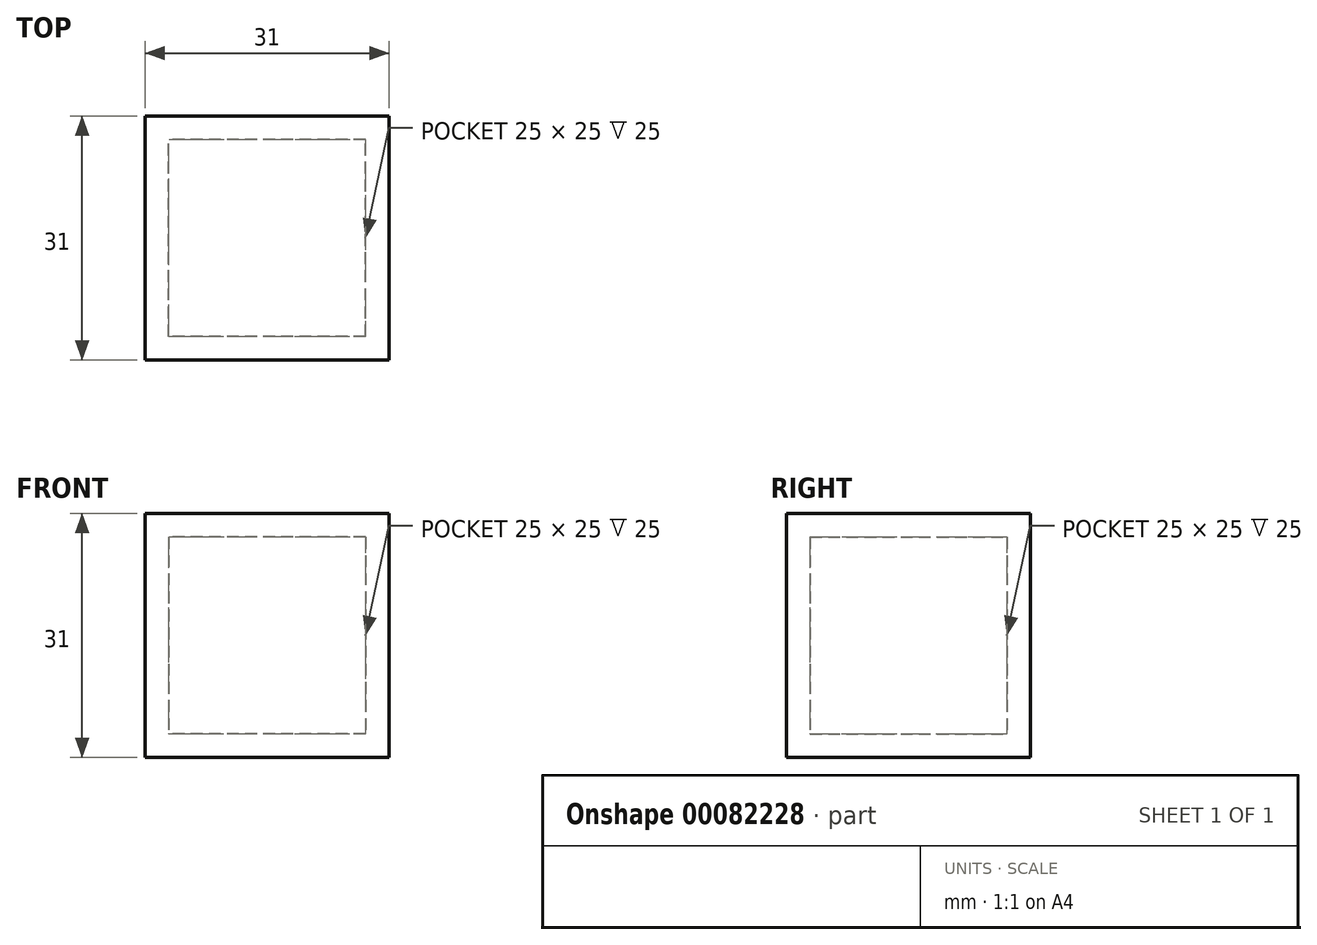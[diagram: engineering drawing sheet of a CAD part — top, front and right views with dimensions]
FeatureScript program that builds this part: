
annotation { "Feature Type Name" : "Feature", "Feature Type Description" : "" }
export const myFeature = defineFeature(function(context is Context, id is Id, definition is map)
    precondition{}
    {
        {
            var Q0;
            Q0=qCreatedBy(makeId("Front.planeOp"),FACE);
            var sketch = newSketch(context, id + "F0", { "sketchPlane" : qUnion([Q0])});
            skLineSegment(sketch, "E0.bottom", {"start": v(12.5, 12.5) * mm, "end": v(-12.5, 12.5) * mm});
            skLineSegment(sketch, "E0.top", {"start": v(12.5, -12.5) * mm, "end": v(-12.5, -12.5) * mm});
            skLineSegment(sketch, "E0.left", {"start": v(12.5, 12.5) * mm, "end": v(12.5, -12.5) * mm});
            skLineSegment(sketch, "E0.right", {"start": v(-12.5, 12.5) * mm, "end": v(-12.5, -12.5) * mm});
            skPoint(sketch, "E0.middle", {"position": v(0, 0) * mm});
            skLineSegment(sketch, "E1.bottom", {"start": v(15.5, 15.5) * mm, "end": v(-15.5, 15.5) * mm});
            skLineSegment(sketch, "E1.top", {"start": v(15.5, -15.5) * mm, "end": v(-15.5, -15.5) * mm});
            skLineSegment(sketch, "E1.left", {"start": v(15.5, 15.5) * mm, "end": v(15.5, -15.5) * mm});
            skLineSegment(sketch, "E1.right", {"start": v(-15.5, 15.5) * mm, "end": v(-15.5, -15.5) * mm});
            skSolve(sketch);
        }
        {
            var Q0;
            Q0 = qSketchRegion(id + "F0", true);
            extrude(context, id + "F1", {"entities" : qUnion([Q0]), "endBound" : BoundingType.SYMMETRIC, "depth" : 31 * mm});
        }
        {
            var Q0;
            Q0=makeQuery(id+"F1.opExtrude","CAP_FACE",FACE,{"disambiguationData":[OSD([sQuery(id+"F0.wireOp",EDGE,"E0.bottom"),sQuery(id+"F0.wireOp",EDGE,"E0.top"),sQuery(id+"F0.wireOp",EDGE,"E0.left"),sQuery(id+"F0.wireOp",EDGE,"E0.right"),sQuery(id+"F0.wireOp",EDGE,"E1.bottom"),sQuery(id+"F0.wireOp",EDGE,"E1.top"),sQuery(id+"F0.wireOp",EDGE,"E1.left"),sQuery(id+"F0.wireOp",EDGE,"E1.right")])],"isStart":false});
            var sketch = newSketch(context, id + "F2", { "sketchPlane" : qUnion([Q0])});
            skLineSegment(sketch, "E2.bottom", {"start": v(12.5, 12.5) * mm, "end": v(-12.5, 12.5) * mm});
            skLineSegment(sketch, "E2.top", {"start": v(12.5, -12.5) * mm, "end": v(-12.5, -12.5) * mm});
            skLineSegment(sketch, "E2.left", {"start": v(12.5, 12.5) * mm, "end": v(12.5, -12.5) * mm});
            skLineSegment(sketch, "E2.right", {"start": v(-12.5, 12.5) * mm, "end": v(-12.5, -12.5) * mm});
            skPoint(sketch, "E2.middle", {"position": v(0, 0) * mm});
            skSolve(sketch);
        }
        {
            var Q0;
            Q0 = qSketchRegion(id + "F2", true);
            extrude(context, id + "F3", {"entities" : qUnion([Q0]), "operationType" : NewBodyOperationType.ADD, "oppositeDirection" : true, "depth" : 3 * mm});
        }
        {
            var Q0;
            Q0=makeQuery(id+"F1.opExtrude","CAP_FACE",FACE,{"disambiguationData":[OSD([sQuery(id+"F0.wireOp",EDGE,"E0.bottom"),sQuery(id+"F0.wireOp",EDGE,"E0.top"),sQuery(id+"F0.wireOp",EDGE,"E0.left"),sQuery(id+"F0.wireOp",EDGE,"E0.right"),sQuery(id+"F0.wireOp",EDGE,"E1.bottom"),sQuery(id+"F0.wireOp",EDGE,"E1.top"),sQuery(id+"F0.wireOp",EDGE,"E1.left"),sQuery(id+"F0.wireOp",EDGE,"E1.right")])],"isStart":true});
            var sketch = newSketch(context, id + "F4", { "sketchPlane" : qUnion([Q0])});
            skLineSegment(sketch, "E3.bottom", {"start": v(12.5, 12.5) * mm, "end": v(-12.5, 12.5) * mm});
            skLineSegment(sketch, "E3.top", {"start": v(12.5, -12.5) * mm, "end": v(-12.5, -12.5) * mm});
            skLineSegment(sketch, "E3.left", {"start": v(12.5, 12.5) * mm, "end": v(12.5, -12.5) * mm});
            skLineSegment(sketch, "E3.right", {"start": v(-12.5, 12.5) * mm, "end": v(-12.5, -12.5) * mm});
            skPoint(sketch, "E3.middle", {"position": v(0, 0) * mm});
            skSolve(sketch);
        }
        {
            var Q0;
            Q0 = qSketchRegion(id + "F4", true);
            extrude(context, id + "F5", {"entities" : qUnion([Q0]), "operationType" : NewBodyOperationType.ADD, "oppositeDirection" : true, "depth" : 3 * mm});
        }
    });
